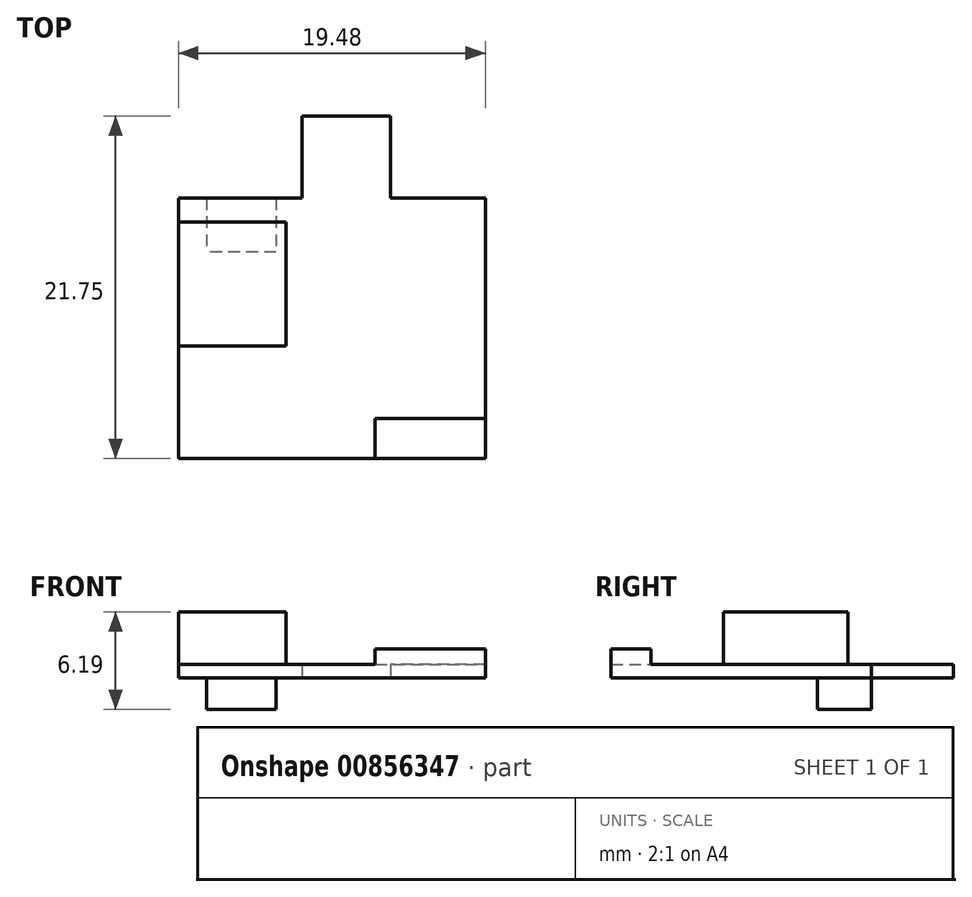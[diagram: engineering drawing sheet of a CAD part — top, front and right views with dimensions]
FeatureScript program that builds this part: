
annotation { "Feature Type Name" : "Feature", "Feature Type Description" : "" }
export const myFeature = defineFeature(function(context is Context, id is Id, definition is map)
    precondition{}
    {
        {
            var Q0;
            Q0=qCreatedBy(makeId("Top.planeOp"),FACE);
            var sketch = newSketch(context, id + "F0", { "sketchPlane" : qUnion([Q0])});
            skLineSegment(sketch, "E0.bottom", {"start": v(9.74, -8.27) * mm, "end": v(-9.74, -8.27) * mm});
            skLineSegment(sketch, "E0.top", {"start": v(9.74, 8.27) * mm, "end": v(3.73, 8.27) * mm});
            skLineSegment(sketch, "E0.left", {"start": v(9.74, -8.27) * mm, "end": v(9.74, 8.27) * mm});
            skLineSegment(sketch, "E0.right", {"start": v(-9.74, -8.27) * mm, "end": v(-9.74, 8.27) * mm});
            skPoint(sketch, "E0.middle", {"position": v(0, 0) * mm});
            skLineSegment(sketch, "E1.top", {"start": v(-1.9, 13.48) * mm, "end": v(3.73, 13.48) * mm});
            skLineSegment(sketch, "E1.left", {"start": v(-1.9, 8.27) * mm, "end": v(-1.9, 13.48) * mm});
            skLineSegment(sketch, "E1.right", {"start": v(3.73, 8.27) * mm, "end": v(3.73, 13.48) * mm});
            skLineSegment(sketch, "E2.trimOffspring", {"start": v(-1.9, 8.27) * mm, "end": v(-9.74, 8.27) * mm});
            skSolve(sketch);
        }
        {
            var Q0;
            Q0 = qSketchRegion(id + "F0", true);
            extrude(context, id + "F1", {"entities" : qUnion([Q0]), "depth" : .85 * mm, "offsetDistance" : 25 * mm});
        }
        {
            var Q0;
            Q0=makeQuery(id+"F1.opExtrude","CAP_FACE",FACE,{"disambiguationData":[OSD([sQuery(id+"F0.wireOp",EDGE,"E0.bottom"),sQuery(id+"F0.wireOp",EDGE,"E0.top"),sQuery(id+"F0.wireOp",EDGE,"E0.left"),sQuery(id+"F0.wireOp",EDGE,"E0.right"),sQuery(id+"F0.wireOp",EDGE,"E1.top"),sQuery(id+"F0.wireOp",EDGE,"E1.left"),sQuery(id+"F0.wireOp",EDGE,"E1.right"),sQuery(id+"F0.wireOp",EDGE,"E2.trimOffspring")])],"isStart":false});
            var sketch = newSketch(context, id + "F2", { "sketchPlane" : qUnion([Q0])});
            skLineSegment(sketch, "E3.bottom", {"start": v(-9.74, 6.75) * mm, "end": v(-2.9, 6.75) * mm});
            skLineSegment(sketch, "E3.top", {"start": v(-9.74, -1.13) * mm, "end": v(-2.9, -1.13) * mm});
            skLineSegment(sketch, "E3.left", {"start": v(-9.74, 6.75) * mm, "end": v(-9.74, -1.13) * mm});
            skLineSegment(sketch, "E3.right", {"start": v(-2.9, 6.75) * mm, "end": v(-2.9, -1.13) * mm});
            skSolve(sketch);
        }
        {
            var Q0;
            Q0 = qSketchRegion(id + "F2", true);
            extrude(context, id + "F3", {"entities" : qUnion([Q0]), "operationType" : NewBodyOperationType.ADD, "depth" : 3.34 * mm, "offsetDistance" : 25 * mm});
        }
        {
            var Q0;
            Q0=makeQuery(id+"F1.opExtrude","CAP_FACE",FACE,{"disambiguationData":[OSD([sQuery(id+"F0.wireOp",EDGE,"E0.bottom"),sQuery(id+"F0.wireOp",EDGE,"E0.top"),sQuery(id+"F0.wireOp",EDGE,"E0.left"),sQuery(id+"F0.wireOp",EDGE,"E0.right"),sQuery(id+"F0.wireOp",EDGE,"E1.top"),sQuery(id+"F0.wireOp",EDGE,"E1.left"),sQuery(id+"F0.wireOp",EDGE,"E1.right"),sQuery(id+"F0.wireOp",EDGE,"E2.trimOffspring")])],"isStart":false});
            var sketch = newSketch(context, id + "F4", { "sketchPlane" : qUnion([Q0])});
            skLineSegment(sketch, "E4.bottom", {"start": v(2.74, -8.27) * mm, "end": v(9.74, -8.27) * mm});
            skLineSegment(sketch, "E4.top", {"start": v(2.74, -5.73) * mm, "end": v(9.74, -5.73) * mm});
            skLineSegment(sketch, "E4.left", {"start": v(2.74, -8.27) * mm, "end": v(2.74, -5.73) * mm});
            skLineSegment(sketch, "E4.right", {"start": v(9.74, -8.27) * mm, "end": v(9.74, -5.73) * mm});
            skSolve(sketch);
        }
        {
            var Q0;
            Q0 = qSketchRegion(id + "F4", true);
            extrude(context, id + "F5", {"entities" : qUnion([Q0]), "operationType" : NewBodyOperationType.ADD, "depth" : 1 * mm, "offsetDistance" : 25 * mm});
        }
        {
            var Q0;
            Q0=makeQuery(id+"F1.opExtrude","CAP_FACE",FACE,{"disambiguationData":[OSD([sQuery(id+"F0.wireOp",EDGE,"E0.bottom"),sQuery(id+"F0.wireOp",EDGE,"E0.top"),sQuery(id+"F0.wireOp",EDGE,"E0.left"),sQuery(id+"F0.wireOp",EDGE,"E0.right"),sQuery(id+"F0.wireOp",EDGE,"E1.top"),sQuery(id+"F0.wireOp",EDGE,"E1.left"),sQuery(id+"F0.wireOp",EDGE,"E1.right"),sQuery(id+"F0.wireOp",EDGE,"E2.trimOffspring")])],"isStart":true});
            var sketch = newSketch(context, id + "F6", { "sketchPlane" : qUnion([Q0])});
            skLineSegment(sketch, "E5.bottom", {"start": v(-3.54, -8.27) * mm, "end": v(-7.97, -8.27) * mm});
            skLineSegment(sketch, "E5.top", {"start": v(-3.54, -4.84) * mm, "end": v(-7.97, -4.84) * mm});
            skLineSegment(sketch, "E5.left", {"start": v(-3.54, -8.27) * mm, "end": v(-3.54, -4.84) * mm});
            skLineSegment(sketch, "E5.right", {"start": v(-7.97, -8.27) * mm, "end": v(-7.97, -4.84) * mm});
            skSolve(sketch);
        }
        {
            var Q0;
            Q0 = qSketchRegion(id + "F6", true);
            extrude(context, id + "F7", {"entities" : qUnion([Q0]), "operationType" : NewBodyOperationType.ADD, "depth" : 2 * mm, "offsetDistance" : 25 * mm});
        }
    });
